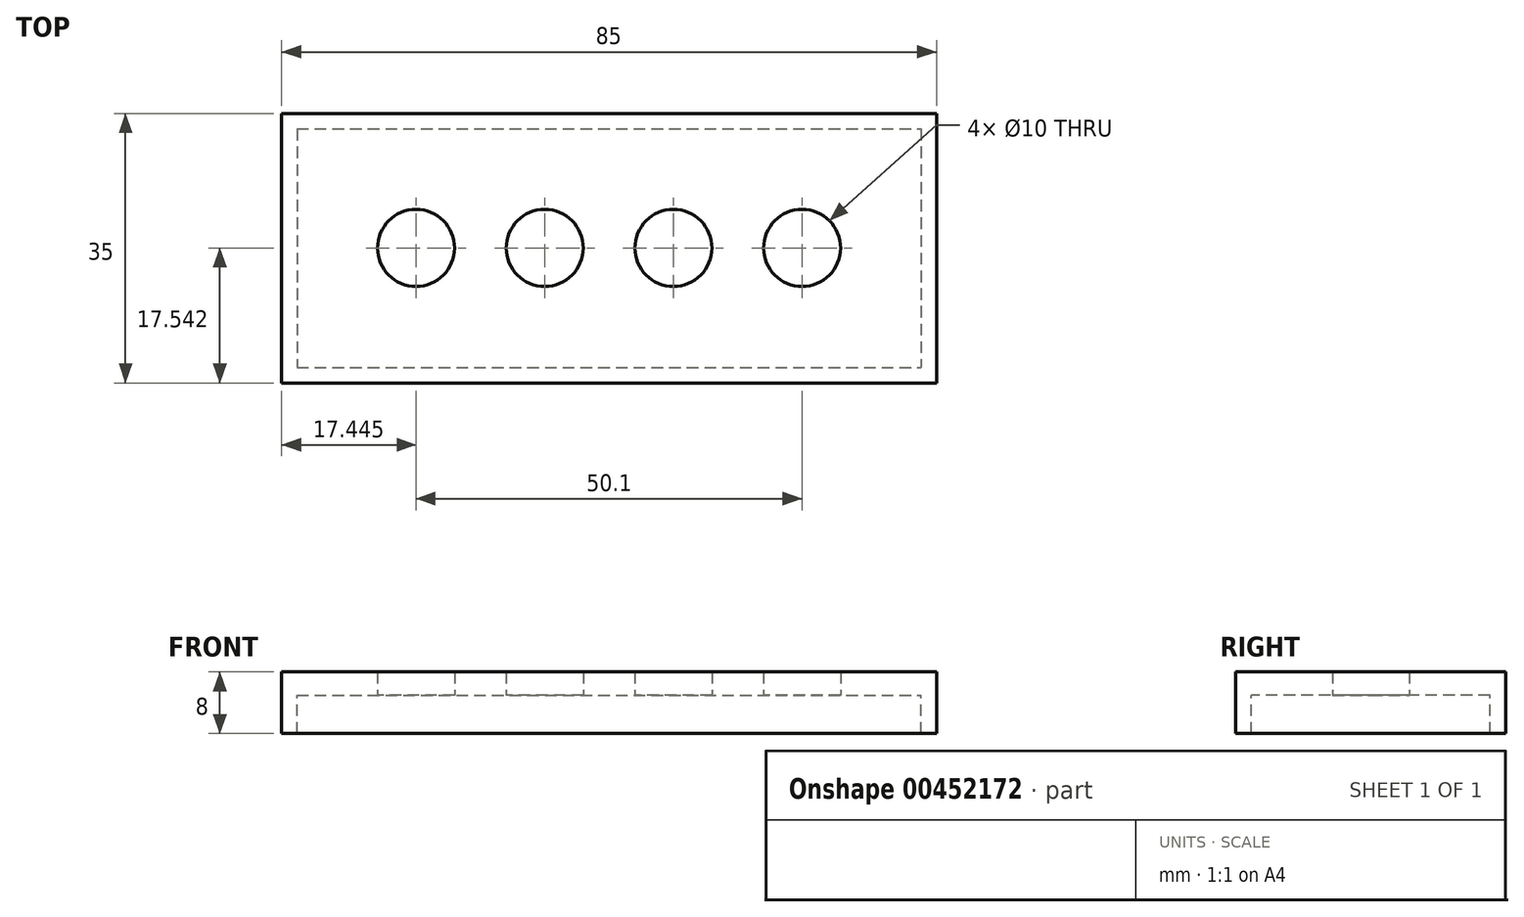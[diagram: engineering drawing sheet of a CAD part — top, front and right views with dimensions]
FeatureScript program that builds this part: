
annotation { "Feature Type Name" : "Feature", "Feature Type Description" : "" }
export const myFeature = defineFeature(function(context is Context, id is Id, definition is map)
    precondition{}
    {
        {
            var Q0;
            Q0=qCreatedBy(makeId("Top.planeOp"),FACE);
            var sketch = newSketch(context, id + "F0", { "sketchPlane" : qUnion([Q0])});
            skLineSegment(sketch, "E0.bottom", {"start": v(-37.43, 12.64) * mm, "end": v(37.57, 12.64) * mm});
            skLineSegment(sketch, "E0.top", {"start": v(-37.43, -12.36) * mm, "end": v(37.57, -12.36) * mm});
            skLineSegment(sketch, "E0.left", {"start": v(-37.43, 12.64) * mm, "end": v(-37.43, -12.36) * mm});
            skLineSegment(sketch, "E0.right", {"start": v(37.57, 12.64) * mm, "end": v(37.57, -12.36) * mm});
            skLineSegment(sketch, "E1", {"start": v(-37.43, 0.14) * mm, "end": v(37.57, 0.14) * mm, "construction": true});
            skLineSegment(sketch, "E2", {"start": v(0.02, 12.64) * mm, "end": v(0.02, -12.36) * mm, "construction": true});
            skLineSegment(sketch, "E3", {"start": v(-24.98, 12.64) * mm, "end": v(-24.98, -12.44) * mm, "construction": true});
            skCircle(sketch, "E4", {"center": v(-24.98, 0.18) * mm, "radius": 5 * mm});
            skCircle(sketch, "E5.1.0.0", {"center": v(-8.28, 0.18) * mm, "radius": 5 * mm});
            skCircle(sketch, "E5.2.0.0", {"center": v(8.42, 0.18) * mm, "radius": 5 * mm});
            skCircle(sketch, "E5.3.0.0", {"center": v(25.12, 0.18) * mm, "radius": 5 * mm});
            skLineSegment(sketch, "E5.direction1", {"start": v(-24.98, 0.18) * mm, "end": v(-8.28, 0.18) * mm, "construction": true});
            skLineSegment(sketch, "E6", {"start": v(25.12, -12.36) * mm, "end": v(25.12, 12.64) * mm, "construction": true});
            skLineSegment(sketch, "E7.0", {"start": v(-42.43, 17.64) * mm, "end": v(42.57, 17.64) * mm});
            skLineSegment(sketch, "E7.1", {"start": v(-42.43, 17.64) * mm, "end": v(-42.43, -17.36) * mm});
            skLineSegment(sketch, "E7.2", {"start": v(-42.43, -17.36) * mm, "end": v(42.57, -17.36) * mm});
            skLineSegment(sketch, "E7.3", {"start": v(42.57, 17.64) * mm, "end": v(42.57, -17.36) * mm});
            skSolve(sketch);
        }
        {
            var Q0;
            Q0=makeQuery(id+"F0.imprint","IMPRINT",FACE,{"disambiguationData":[TD([[makeQuery(id+"F0.imprint","IMPRINT",EDGE,{"derivedFrom":sQuery(id+"F0.wireOp",EDGE,"E0.bottom")}),-1.0]])]});
            extrude(context, id + "F1", {"entities" : qUnion([Q0]), "depth" : 3 * mm});
        }
        {
            var Q0;
            Q0 = qSketchRegion(id + "F0", true);
            extrude(context, id + "F2", {"entities" : qUnion([Q0]), "operationType" : NewBodyOperationType.ADD, "depth" : 3 * mm});
        }
        {
            var Q0;
            {var subQ0=sQuery(id+"F0.wireOp",EDGE,"E0.right");var subQ1=sQuery(id+"F0.wireOp",EDGE,"E0.left");var subQ2=sQuery(id+"F0.wireOp",EDGE,"E0.top");var subQ3=sQuery(id+"F0.wireOp",EDGE,"E0.bottom");Q0=makeQuery(id+"F2.boolean.opBoolean","MERGE",FACE,{"derivedFrom":[makeQuery(id+"F1.opExtrude","CAP_FACE",FACE,{"disambiguationData":[OSD([subQ3,subQ2,subQ1,subQ0,sQuery(id+"F0.wireOp",EDGE,"E4"),sQuery(id+"F0.wireOp",EDGE,"E5.1.0.0"),sQuery(id+"F0.wireOp",EDGE,"E5.2.0.0"),sQuery(id+"F0.wireOp",EDGE,"E5.3.0.0")])],"isStart":true}),makeQuery(id+"F2.opExtrude","CAP_FACE",FACE,{"disambiguationData":[OSD([subQ3,subQ2,subQ1,subQ0,sQuery(id+"F0.wireOp",EDGE,"E7.0"),sQuery(id+"F0.wireOp",EDGE,"E7.1"),sQuery(id+"F0.wireOp",EDGE,"E7.2"),sQuery(id+"F0.wireOp",EDGE,"E7.3")])],"isStart":true})]});}
            var sketch = newSketch(context, id + "F3", { "sketchPlane" : qUnion([Q0])});
            skLineSegment(sketch, "E8.0", {"start": v(-40.43, 15.36) * mm, "end": v(40.57, 15.36) * mm});
            skLineSegment(sketch, "E8.1", {"start": v(-40.43, -15.64) * mm, "end": v(-40.43, 15.36) * mm});
            skLineSegment(sketch, "E8.2", {"start": v(-40.43, -15.64) * mm, "end": v(40.57, -15.64) * mm});
            skLineSegment(sketch, "E8.3", {"start": v(40.57, -15.64) * mm, "end": v(40.57, 15.36) * mm});
            skSolve(sketch);
        }
        {
            var Q0;
            Q0=makeQuery(id+"F3.imprint","IMPRINT",FACE,{"disambiguationData":[TD([[makeQuery(id+"F3.imprint","IMPRINT",EDGE,{"derivedFrom":sQuery(id+"F3.wireOp",EDGE,"E8.0")}),1.0]])]});
            extrude(context, id + "F4", {"entities" : qUnion([Q0]), "operationType" : NewBodyOperationType.ADD, "depth" : 5 * mm});
        }
    });
